# Revit family: Shower-Valve_Trim-KOHLER-Aleo-K-72291M
name_source: partatom
category: Specialty Equipment
revit_build: Autodesk Revit 2017 (Build: 20160225_1515(x64)
units: mm (PartAtom-declared; Revit-internal decimal feet)

## family parameters
Cut with Voids When Loaded = No
Host = Face
OmniClass Number = 23.31.25.00
Part Type = Normal
Room Calculation Point = No
Round Connector Dimension = Use Diameter
Shared = No

## types (1)
- CP- Polished chrome
    ADA Compliant = No
    Assembly Code = C1030200
    Date Modified = 10/08/2020
    Default Elevation = 42"
    Description = shower handle
    Finish = Kohler-Metal-CP-Polished_Chrome
    Height = 6 9/16"
    Length = 3 3/16"
    Manufacturer = KOHLER Co.
    Master Format 2014 = 10 28 00
    Master Format 2014 Name = Toilet, Bath, and Laundry Accessories
    Material = Metal consrtuction
    Model = K-72291M-4-CP
    Product Documentation Link = http://resources.kohler.com
    Product Name = Aleo
    Product Page URL = https://la.kohler.com
    Type = 1
    URL = https://la.kohler.com
    WaterSense Certified = No
    Width = 4 7/16"

## geometry (parser evidence)
native form markers: Sweep x6
no freeform markers — native parametric forms only
